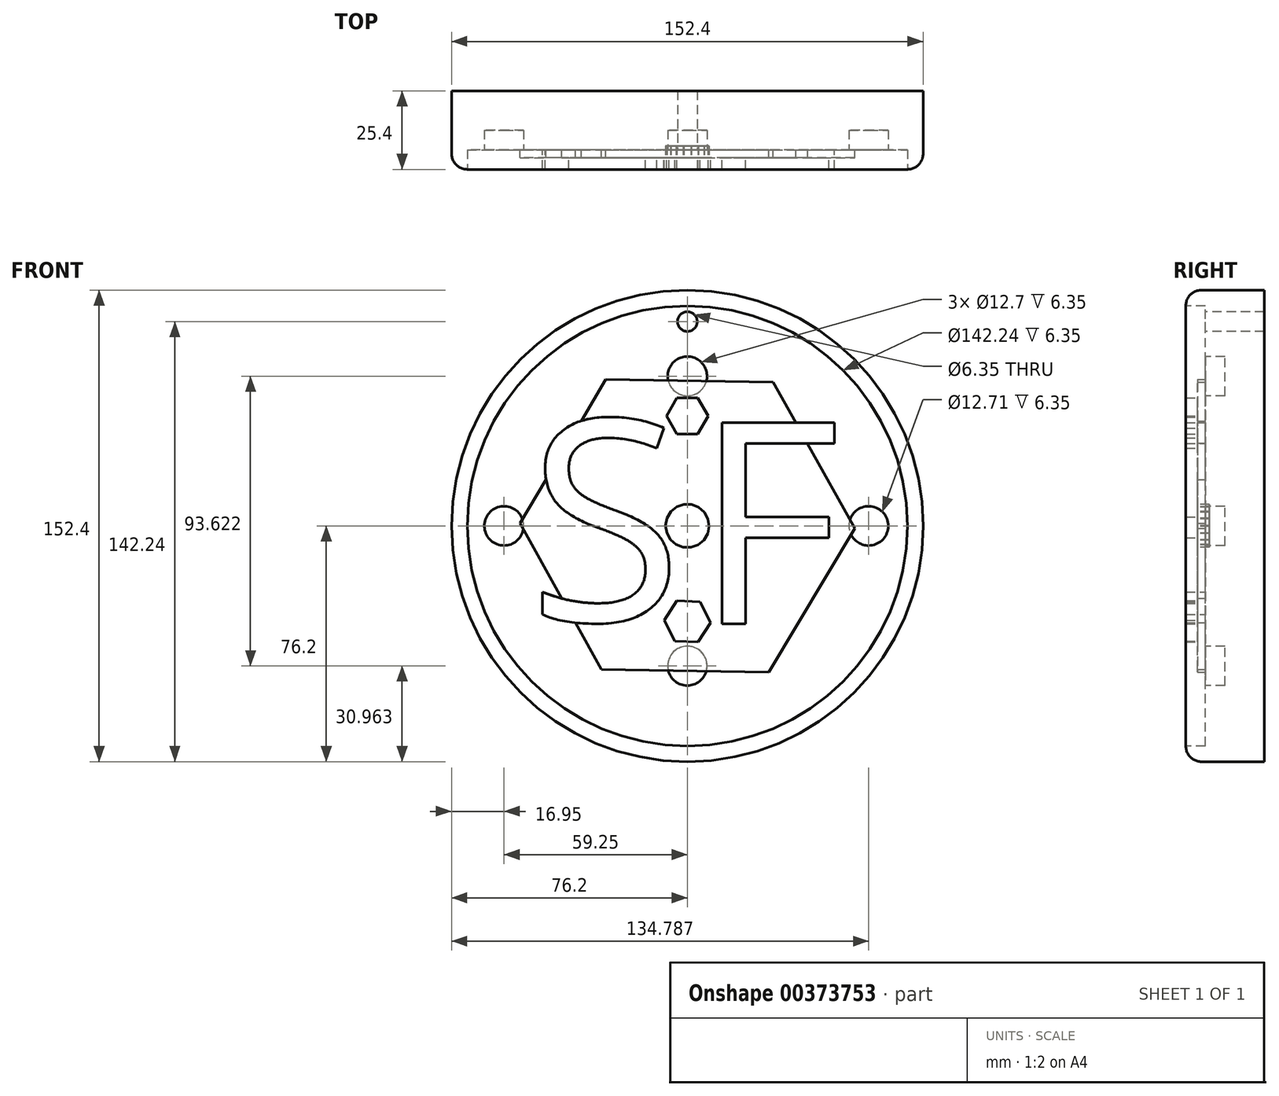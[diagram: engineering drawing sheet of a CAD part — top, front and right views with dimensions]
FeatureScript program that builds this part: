
annotation { "Feature Type Name" : "Feature", "Feature Type Description" : "" }
export const myFeature = defineFeature(function(context is Context, id is Id, definition is map)
    precondition{}
    {
        {
            var Q0;
            Q0=qCreatedBy(makeId("Front.planeOp"),FACE);
            var sketch = newSketch(context, id + "F0", { "sketchPlane" : qUnion([Q0])});
            skCircle(sketch, "E0", {"center": v(0, 0) * mm, "radius": 76.2 * mm});
            skSolve(sketch);
        }
        {
            var Q0;
            Q0 = qSketchRegion(id + "F0", true);
            extrude(context, id + "F1", {"entities" : qUnion([Q0]), "depth" : 25.4 * mm});
        }
        {
            var Q0;
            Q0=makeQuery(id+"F1.opExtrude","CAP_EDGE",EDGE,{"disambiguationData":[OSD([sQuery(id+"F0.wireOp",EDGE,"E0")])],"isStart":false});
            fillet(context, id + "F2", {"entities" : qUnion([Q0]), "radius" : 5.08 * mm, "tangentPropagation" : true, "allowEdgeOverflow" : false});
        }
        {
            var Q0;
            Q0=makeQuery(id+"F1.opExtrude","CAP_FACE",FACE,{"disambiguationData":[OSD([sQuery(id+"F0.wireOp",EDGE,"E0")])],"isStart":false});
            extrude(context, id + "F3", {"entities" : qUnion([Q0]), "operationType" : NewBodyOperationType.REMOVE, "oppositeDirection" : true, "depth" : 6.35 * mm});
        }
        {
            var Q0;
            Q0=makeQuery(id+"F3.boolean.opBoolean","COPY",FACE,{"derivedFrom":makeQuery(id+"F3.opExtrude","CAP_FACE",FACE,{"disambiguationData":[OSD([sQuery(id+"F0.wireOp",EDGE,"E0")])],"isStart":false})});
            var sketch = newSketch(context, id + "F4", { "sketchPlane" : qUnion([Q0])});
            skText(sketch, "E1", { "text": "S", "fontName": "OpenSans-Regular.ttf"});
            const initialGuessF4  = {"E1": [-0.05153, -0.03075, 1, 0, 0.06558]};
            skSetInitialGuess(sketch, initialGuessF4);
            skSolve(sketch);
        }
        {
            var Q0;
            Q0 = qSketchRegion(id + "F4", true);
            extrude(context, id + "F5", {"entities" : qUnion([Q0]), "operationType" : NewBodyOperationType.ADD, "depth" : 6.35 * mm});
        }
        {
            var Q0;
            Q0=makeQuery(id+"F3.boolean.opBoolean","COPY",FACE,{"derivedFrom":makeQuery(id+"F3.opExtrude","CAP_FACE",FACE,{"disambiguationData":[OSD([sQuery(id+"F0.wireOp",EDGE,"E0")])],"isStart":false})});
            var sketch = newSketch(context, id + "F6", { "sketchPlane" : qUnion([Q0])});
            skText(sketch, "E2", { "text": "F", "fontName": "OpenSans-Regular.ttf"});
            const initialGuessF6  = {"E2": [0.00233, -0.03163, 1, 0, 0.06558]};
            skSetInitialGuess(sketch, initialGuessF6);
            skSolve(sketch);
        }
        {
            var Q0;
            Q0 = qSketchRegion(id + "F6", true);
            extrude(context, id + "F7", {"entities" : qUnion([Q0]), "operationType" : NewBodyOperationType.ADD, "depth" : 6.35 * mm});
        }
        {
            var Q0;
            Q0=makeQuery(id+"F3.boolean.opBoolean","COPY",FACE,{"derivedFrom":makeQuery(id+"F3.opExtrude","CAP_FACE",FACE,{"disambiguationData":[OSD([sQuery(id+"F0.wireOp",EDGE,"E0")])],"isStart":false})});
            var sketch = newSketch(context, id + "F8", { "sketchPlane" : qUnion([Q0])});
            skCircle(sketch, "E3", {"center": v(0, 66.04) * mm, "radius": 3.18 * mm});
            skSolve(sketch);
        }
        {
            var Q0;
            Q0 = qSketchRegion(id + "F8", true);
            extrude(context, id + "F9", {"entities" : qUnion([Q0]), "operationType" : NewBodyOperationType.REMOVE, "oppositeDirection" : true, "depth" : 50.8 * mm});
        }
        {
            var Q0;
            Q0=makeQuery(id+"F3.boolean.opBoolean","COPY",FACE,{"derivedFrom":makeQuery(id+"F3.opExtrude","CAP_FACE",FACE,{"disambiguationData":[OSD([sQuery(id+"F0.wireOp",EDGE,"E0")])],"isStart":false})});
            var sketch = newSketch(context, id + "F10", { "sketchPlane" : qUnion([Q0])});
            skCircle(sketch, "E4", {"center": v(0, 48.38) * mm, "radius": 6.35 * mm});
            skSolve(sketch);
        }
        {
            var Q0;
            Q0 = qSketchRegion(id + "F10", true);
            extrude(context, id + "F11", {"entities" : qUnion([Q0]), "operationType" : NewBodyOperationType.REMOVE, "oppositeDirection" : true, "depth" : 6.35 * mm});
        }
        {
            var Q0;
            Q0=makeQuery(id+"F3.boolean.opBoolean","COPY",FACE,{"derivedFrom":makeQuery(id+"F3.opExtrude","CAP_FACE",FACE,{"disambiguationData":[OSD([sQuery(id+"F0.wireOp",EDGE,"E0")])],"isStart":false})});
            var sketch = newSketch(context, id + "F12", { "sketchPlane" : qUnion([Q0])});
            skCircle(sketch, "E5", {"center": v(0, -45.24) * mm, "radius": 6.35 * mm});
            skSolve(sketch);
        }
        {
            var Q0;
            Q0 = qSketchRegion(id + "F12", true);
            extrude(context, id + "F13", {"entities" : qUnion([Q0]), "operationType" : NewBodyOperationType.REMOVE, "oppositeDirection" : true, "depth" : 6.35 * mm});
        }
        {
            var Q0;
            Q0=makeQuery(id+"F3.boolean.opBoolean","COPY",FACE,{"derivedFrom":makeQuery(id+"F3.opExtrude","CAP_FACE",FACE,{"disambiguationData":[OSD([sQuery(id+"F0.wireOp",EDGE,"E0")])],"isStart":false})});
            var sketch = newSketch(context, id + "F14", { "sketchPlane" : qUnion([Q0])});
            skCircle(sketch, "E6", {"center": v(-59.25, 0) * mm, "radius": 6.35 * mm});
            skSolve(sketch);
        }
        {
            var Q0;
            Q0 = qSketchRegion(id + "F14", true);
            extrude(context, id + "F15", {"entities" : qUnion([Q0]), "operationType" : NewBodyOperationType.REMOVE, "oppositeDirection" : true, "depth" : 6.35 * mm});
        }
        {
            var Q0;
            Q0=makeQuery(id+"F3.boolean.opBoolean","COPY",FACE,{"derivedFrom":makeQuery(id+"F3.opExtrude","CAP_FACE",FACE,{"disambiguationData":[OSD([sQuery(id+"F0.wireOp",EDGE,"E0")])],"isStart":false})});
            var sketch = newSketch(context, id + "F16", { "sketchPlane" : qUnion([Q0])});
            skCircle(sketch, "E7", {"center": v(58.59, 0) * mm, "radius": 6.35 * mm});
            skSolve(sketch);
        }
        {
            var Q0;
            Q0 = qSketchRegion(id + "F16", true);
            extrude(context, id + "F17", {"entities" : qUnion([Q0]), "operationType" : NewBodyOperationType.REMOVE, "oppositeDirection" : true, "depth" : 6.35 * mm});
        }
        {
            var Q0;
            Q0=makeQuery(id+"F3.boolean.opBoolean","COPY",FACE,{"derivedFrom":makeQuery(id+"F3.opExtrude","CAP_FACE",FACE,{"disambiguationData":[OSD([sQuery(id+"F0.wireOp",EDGE,"E0")])],"isStart":false})});
            var sketch = newSketch(context, id + "F18", { "sketchPlane" : qUnion([Q0])});
            skSolve(sketch);
        }
        {
            var Q0;
            Q0=makeQuery(id+"F18.imprint","IMPRINT",FACE,{"disambiguationData":[TD([[makeQuery(id+"F18.imprint","IMPRINT",EDGE,{"derivedFrom":makeQuery(id+"F3.boolean.opBoolean","COPY",EDGE,{"derivedFrom":makeQuery(id+"F3.opExtrude","CAP_EDGE",EDGE,{"disambiguationData":[OSD([sQuery(id+"F0.wireOp",EDGE,"E0")])],"isStart":false})})}),1.0]])]});
            var sketch = newSketch(context, id + "F19", { "sketchPlane" : qUnion([Q0])});
            skCircle(sketch, "E8.cCircle", {"center": v(0, 0) * mm, "radius": 46.86 * mm, "construction": true});
            skLineSegment(sketch, "E8.0", {"start": v(54.1, -0.82) * mm, "end": v(26.34, -47.27) * mm});
            skLineSegment(sketch, "E8.1", {"start": v(26.34, -47.27) * mm, "end": v(-27.77, -46.45) * mm});
            skLineSegment(sketch, "E8.2", {"start": v(-27.77, -46.45) * mm, "end": v(-54.1, 0.82) * mm});
            skLineSegment(sketch, "E8.3", {"start": v(-54.1, 0.82) * mm, "end": v(-26.34, 47.27) * mm});
            skLineSegment(sketch, "E8.4", {"start": v(-26.34, 47.27) * mm, "end": v(27.77, 46.45) * mm});
            skLineSegment(sketch, "E8.5", {"start": v(27.77, 46.45) * mm, "end": v(54.1, -0.82) * mm});
            skPoint(sketch, "E8.0.midPoint", {"position": v(40.22, -24.05) * mm});
            skSolve(sketch);
        }
        {
            var Q0;
            Q0 = qSketchRegion(id + "F19", true);
            extrude(context, id + "F20", {"entities" : qUnion([Q0]), "operationType" : NewBodyOperationType.ADD, "depth" : 2.54 * mm});
        }
        {
            var Q0;
            {var subQ0=sQuery(id+"F19.wireOp",EDGE,"E8.4");var subQ1=sQuery(id+"F19.wireOp",EDGE,"E8.3");var subQ2=sQuery(id+"F19.wireOp",EDGE,"E8.0");var subQ3=sQuery(id+"F19.wireOp",EDGE,"E8.1");var subQ4=sQuery(id+"F19.wireOp",EDGE,"E8.2");var subQ5=sQuery(id+"F19.wireOp",EDGE,"E8.5");Q0=makeQuery(id+"F20.boolean.opBoolean","SPLIT",FACE,{"disambiguationData":[TD([makeQuery(id+"F5.opExtrude","SWEPT_FACE",FACE,{"disambiguationData":[OSD([sQuery(id+"F4.wireOp",EDGE,"E1.sketch_text.stroke-0")])]})])],"derivedFrom":makeQuery(id+"F20.opExtrude","CAP_FACE",FACE,{"disambiguationData":[OSD([subQ2,subQ3,subQ4,subQ1,subQ0,subQ5])],"isStart":false})});}
            var sketch = newSketch(context, id + "F21", { "sketchPlane" : qUnion([Q0])});
            skCircle(sketch, "E9.cCircle", {"center": v(0, 0) * mm, "radius": 6.92 * mm, "construction": true});
            skLineSegment(sketch, "E9.0", {"start": v(6.57, -2.5) * mm, "end": v(5.32, -4.6) * mm});
            skLineSegment(sketch, "E9.1", {"start": v(5.32, -4.6) * mm, "end": v(3.42, -6.14) * mm});
            skLineSegment(sketch, "E9.2", {"start": v(3.42, -6.14) * mm, "end": v(1.12, -6.94) * mm});
            skLineSegment(sketch, "E9.3", {"start": v(1.12, -6.94) * mm, "end": v(-1.33, -6.9) * mm});
            skLineSegment(sketch, "E9.4", {"start": v(-1.33, -6.9) * mm, "end": v(-3.6, -6.03) * mm});
            skLineSegment(sketch, "E9.5", {"start": v(-3.6, -6.03) * mm, "end": v(-5.45, -4.44) * mm});
            skLineSegment(sketch, "E9.6", {"start": v(-5.45, -4.44) * mm, "end": v(-6.64, -2.3) * mm});
            skLineSegment(sketch, "E9.7", {"start": v(-6.64, -2.3) * mm, "end": v(-7.03, 0.1) * mm});
            skLineSegment(sketch, "E9.8", {"start": v(-7.03, 0.1) * mm, "end": v(-6.57, 2.5) * mm});
            skLineSegment(sketch, "E9.9", {"start": v(-6.57, 2.5) * mm, "end": v(-5.32, 4.6) * mm});
            skLineSegment(sketch, "E9.10", {"start": v(-5.32, 4.6) * mm, "end": v(-3.42, 6.14) * mm});
            skLineSegment(sketch, "E9.11", {"start": v(-3.42, 6.14) * mm, "end": v(-1.12, 6.94) * mm});
            skLineSegment(sketch, "E9.12", {"start": v(-1.12, 6.94) * mm, "end": v(1.33, 6.9) * mm});
            skLineSegment(sketch, "E9.13", {"start": v(1.33, 6.9) * mm, "end": v(3.6, 6.03) * mm});
            skLineSegment(sketch, "E9.14", {"start": v(3.6, 6.03) * mm, "end": v(5.45, 4.44) * mm});
            skLineSegment(sketch, "E9.15", {"start": v(5.45, 4.44) * mm, "end": v(6.64, 2.3) * mm});
            skLineSegment(sketch, "E9.16", {"start": v(6.64, 2.3) * mm, "end": v(7.03, -0.1) * mm});
            skLineSegment(sketch, "E9.17", {"start": v(7.03, -0.1) * mm, "end": v(6.57, -2.5) * mm});
            skPoint(sketch, "E9.0.midPoint", {"position": v(5.94, -3.55) * mm});
            skSolve(sketch);
        }
        {
            var Q0;
            Q0 = qSketchRegion(id + "F21", true);
            extrude(context, id + "F22", {"entities" : qUnion([Q0]), "operationType" : NewBodyOperationType.REMOVE, "oppositeDirection" : true, "depth" : 3.8 * mm});
        }
        {
            var Q0;
            {var subQ0=sQuery(id+"F19.wireOp",EDGE,"E8.4");var subQ1=sQuery(id+"F19.wireOp",EDGE,"E8.3");var subQ2=sQuery(id+"F19.wireOp",EDGE,"E8.0");var subQ3=sQuery(id+"F19.wireOp",EDGE,"E8.1");var subQ4=sQuery(id+"F19.wireOp",EDGE,"E8.2");var subQ5=sQuery(id+"F19.wireOp",EDGE,"E8.5");Q0=makeQuery(id+"F20.boolean.opBoolean","SPLIT",FACE,{"disambiguationData":[TD([makeQuery(id+"F5.opExtrude","SWEPT_FACE",FACE,{"disambiguationData":[OSD([sQuery(id+"F4.wireOp",EDGE,"E1.sketch_text.stroke-0")])]})])],"derivedFrom":makeQuery(id+"F20.opExtrude","CAP_FACE",FACE,{"disambiguationData":[OSD([subQ2,subQ3,subQ4,subQ1,subQ0,subQ5])],"isStart":false})});}
            var sketch = newSketch(context, id + "F23", { "sketchPlane" : qUnion([Q0])});
            skCircle(sketch, "E10.cCircle", {"center": v(0, -30.88) * mm, "radius": 7.53 * mm, "construction": true});
            skLineSegment(sketch, "E10.0", {"start": v(3.47, -37.57) * mm, "end": v(-4.06, -37.23) * mm});
            skLineSegment(sketch, "E10.1", {"start": v(-4.06, -37.23) * mm, "end": v(-7.52, -30.54) * mm});
            skLineSegment(sketch, "E10.2", {"start": v(-7.52, -30.54) * mm, "end": v(-3.47, -24.2) * mm});
            skLineSegment(sketch, "E10.3", {"start": v(-3.47, -24.2) * mm, "end": v(4.06, -24.54) * mm});
            skLineSegment(sketch, "E10.4", {"start": v(4.06, -24.54) * mm, "end": v(7.52, -31.22) * mm});
            skLineSegment(sketch, "E10.5", {"start": v(7.52, -31.22) * mm, "end": v(3.47, -37.57) * mm});
            skSolve(sketch);
        }
        {
            var Q0;
            Q0 = qSketchRegion(id + "F23", true);
            extrude(context, id + "F24", {"entities" : qUnion([Q0]), "operationType" : NewBodyOperationType.ADD, "depth" : 3.8 * mm});
        }
        {
            var Q0;
            {var subQ0=sQuery(id+"F19.wireOp",EDGE,"E8.4");var subQ1=sQuery(id+"F19.wireOp",EDGE,"E8.3");var subQ2=sQuery(id+"F19.wireOp",EDGE,"E8.0");var subQ3=sQuery(id+"F19.wireOp",EDGE,"E8.1");var subQ4=sQuery(id+"F19.wireOp",EDGE,"E8.2");var subQ5=sQuery(id+"F19.wireOp",EDGE,"E8.5");Q0=makeQuery(id+"F20.boolean.opBoolean","SPLIT",FACE,{"disambiguationData":[TD([makeQuery(id+"F5.opExtrude","SWEPT_FACE",FACE,{"disambiguationData":[OSD([sQuery(id+"F4.wireOp",EDGE,"E1.sketch_text.stroke-0")])]})])],"derivedFrom":makeQuery(id+"F20.opExtrude","CAP_FACE",FACE,{"disambiguationData":[OSD([subQ2,subQ3,subQ4,subQ1,subQ0,subQ5])],"isStart":false})});}
            var sketch = newSketch(context, id + "F25", { "sketchPlane" : qUnion([Q0])});
            skCircle(sketch, "E11.cCircle", {"center": v(0, 35.5) * mm, "radius": 6.72 * mm, "construction": true});
            skLineSegment(sketch, "E11.0", {"start": v(6.72, 35.52) * mm, "end": v(3.38, 29.69) * mm});
            skLineSegment(sketch, "E11.1", {"start": v(3.38, 29.69) * mm, "end": v(-3.34, 29.67) * mm});
            skLineSegment(sketch, "E11.2", {"start": v(-3.34, 29.67) * mm, "end": v(-6.72, 35.48) * mm});
            skLineSegment(sketch, "E11.3", {"start": v(-6.72, 35.48) * mm, "end": v(-3.38, 41.3) * mm});
            skLineSegment(sketch, "E11.4", {"start": v(-3.38, 41.3) * mm, "end": v(3.34, 41.33) * mm});
            skLineSegment(sketch, "E11.5", {"start": v(3.34, 41.33) * mm, "end": v(6.72, 35.52) * mm});
            skSolve(sketch);
        }
        {
            var Q0;
            Q0 = qSketchRegion(id + "F25", true);
            extrude(context, id + "F26", {"entities" : qUnion([Q0]), "operationType" : NewBodyOperationType.ADD, "depth" : 3.8 * mm});
        }
    });
